# Revit family: R1320T
name_source: partatom
category: Plumbing Fixtures
revit_build: Autodesk Revit 2018 (Build: 20170223_1515(x64)
units: mm (PartAtom-declared; Revit-internal decimal feet)

## family parameters
Cut with Voids When Loaded = No
Host = Face
Part Type = Normal
Room Calculation Point = No
Round Connector Dimension = Use Radius
Shared = No

## types (5) — shared parameters
Default Elevation = 0' - 0"
Description = SCUPPER DRAIN WITH FLAT GRATE AND 90 DEGREE THREADED OUTLET
Floor Drain Material = Paint - Sherwin Williams Paint - #952C2A - Bellwood Red
Manufacturer = MIFAB
URL = WWW.MIFAB.COM
zero-valued in all types: CWFU, WFU

## per-type parameters (varying)
| type | A | B | B-Cut | Bottom Height | C | Model | Pipe Diameter | Pipe Radius | T-Cut |
| R1324T - 4" Drain Pipe Size | 0' - 7 1/2" | 0' - 6 3/8" | 0' - 1 1/16" | 0' - 6 5/8" | 0' - 2 3/4" | R1324T | 0' - 4" | 0' - 2" | 0' - 0" |
| R1323T - 3" Drain Pipe Size | 0' - 7 1/2" | 0' - 6 3/8" | 0' - 1 1/16" | 0' - 6 1/8" | 0' - 2 3/4" | R1323T | 0' - 3" | 0' - 1 1/2" | 0' - 0" |
| R1322T - 2" Drain Pipe Size | 0' - 7 1/2" | 0' - 6 3/8" | 0' - 1 1/16" | 0' - 5 5/8" | 0' - 2 3/4" | R1322T | 0' - 2" | 0' - 1" | 0' - 0" |
| R1326T - 6" Drain Pipe Size | 1' - 0 1/2" | 0' - 8 3/8" | 0' - 0" | 0' - 7 5/8" | 0' - 3 1/2" | R1326T | 0' - 6" | 0' - 3" | 0' - 1 7/16" |
| R1328T - 8" Drain Pipe Size | 1' - 0 1/2" | 0' - 8 3/8" | 0' - 0" | 0' - 8 5/8" | 0' - 3 1/2" | R1328T | 0' - 8" | 0' - 4" | 0' - 1 7/16" |

## geometry (parser evidence)
native form markers: Sweep x9
no freeform markers — native parametric forms only
